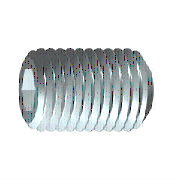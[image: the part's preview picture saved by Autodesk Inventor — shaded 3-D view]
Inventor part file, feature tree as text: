
AUTODESK INVENTOR PART (.ipt)
format: ipt  version: 2017 (Build 210142000, 142)  size: 171,008 bytes
history: native  units: mm (DEFAULTED — no unit token found)
features: sketch x2, extrude x1, other x1, plane x1
ambient origin geometry x8: Origin, YZ Plane, XZ Plane, XY Plane, X Axis, Y Axis, Z Axis, Center Point
bodies: Solid1 (feature_tree), Body (feature_tree)
feature tree (5):
  extrude  "Slot"  TaperAngle=60.0deg  [1 undecoded]
  other  "Work Axis1"
  plane  "Work Plane1"
  sketch  "Sketch1"  dims[d0=2.0mm d1=60.0deg]
  sketch  "Sketch2"  dims[d2=3.0mm d3=1.732051mm d6=90.0deg d4=5.0mm d5=60.0deg d7=2.0mm d8=2.0mm d9=0.0mm d10=0.5mm d11=45.0deg d12=0.306725mm d13=45.0deg d14=5.0mm d15=0.0mm d16=0.0mm d33=0.5mm d34=0.306725mm d35=0.0mm d37=0.0mm]
note: 1 required parameter value undecoded (feature->parameter linkage not recoverable at this tier; creation-order binding heuristic only, values carry confidence <= 0.55)
